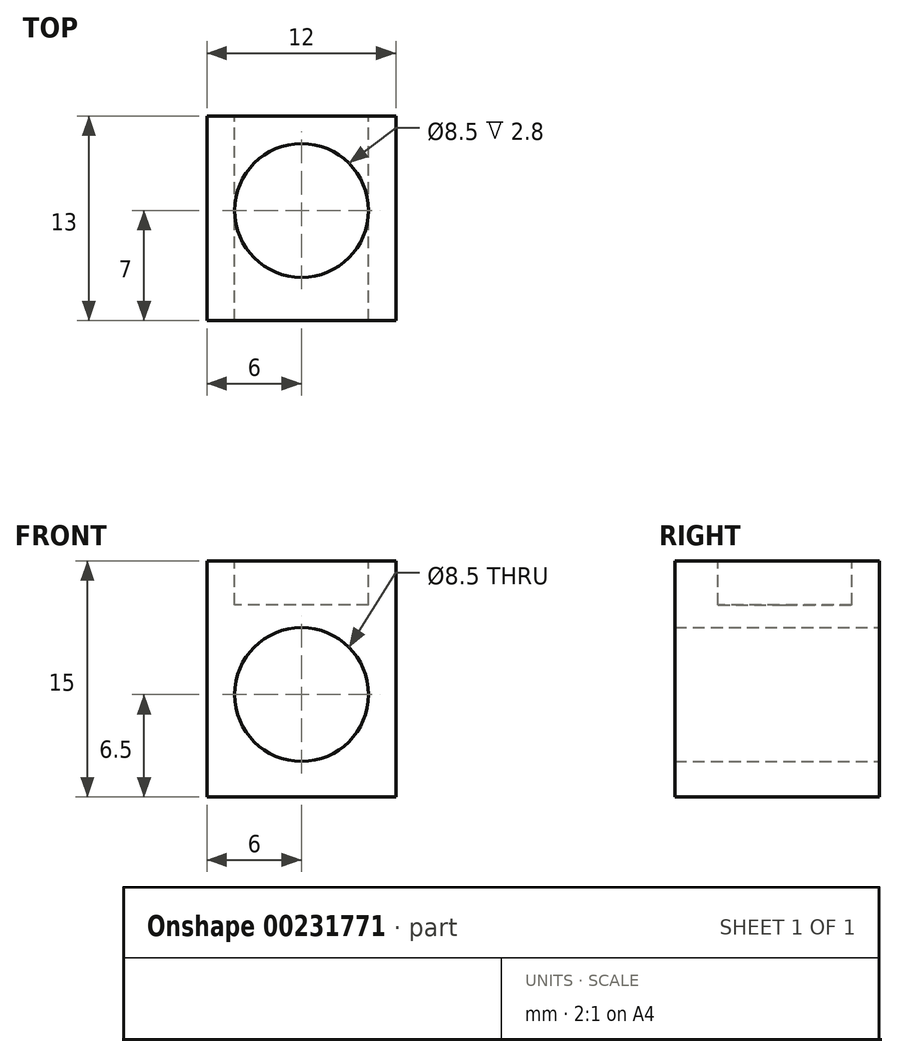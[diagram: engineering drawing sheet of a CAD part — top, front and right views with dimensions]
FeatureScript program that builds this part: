
annotation { "Feature Type Name" : "Feature", "Feature Type Description" : "" }
export const myFeature = defineFeature(function(context is Context, id is Id, definition is map)
    precondition{}
    {
        {
            var Q0;
            Q0=qCreatedBy(makeId("Front.planeOp"),FACE);
            var sketch = newSketch(context, id + "F0", { "sketchPlane" : qUnion([Q0])});
            skLineSegment(sketch, "E0.bottom", {"start": v(-6, 7.5) * mm, "end": v(6, 7.5) * mm});
            skLineSegment(sketch, "E0.top", {"start": v(-6, -7.5) * mm, "end": v(6, -7.5) * mm});
            skLineSegment(sketch, "E0.left", {"start": v(-6, 7.5) * mm, "end": v(-6, -7.5) * mm});
            skLineSegment(sketch, "E0.right", {"start": v(6, 7.5) * mm, "end": v(6, -7.5) * mm});
            skCircle(sketch, "E1", {"center": v(0, -1) * mm, "radius": 4.25 * mm});
            skSolve(sketch);
        }
        {
            var Q0;
            Q0=makeQuery(id+"F0.imprint","IMPRINT",FACE,{"disambiguationData":[TD([[makeQuery(id+"F0.imprint","IMPRINT",EDGE,{"derivedFrom":sQuery(id+"F0.wireOp",EDGE,"E0.bottom")}),-1.0]])]});
            extrude(context, id + "F1", {"entities" : qUnion([Q0]), "depth" : 24 * mm});
        }
        {
            var Q0;
            Q0=makeQuery(id+"F1.opExtrude","SWEPT_FACE",FACE,{"disambiguationData":[OSD([sQuery(id+"F0.wireOp",EDGE,"E0.bottom")])]});
            var sketch = newSketch(context, id + "F2", { "sketchPlane" : qUnion([Q0])});
            skCircle(sketch, "E2", {"center": v(0, -6) * mm, "radius": 4.12 * mm});
            skCircle(sketch, "E3", {"center": v(0, -17) * mm, "radius": 4.25 * mm});
            skSolve(sketch);
        }
        {
            var Q0;
            Q0=makeQuery(id+"F2.imprint","IMPRINT",FACE,{"disambiguationData":[TD([[makeQuery(id+"F2.imprint","IMPRINT",EDGE,{"derivedFrom":sQuery(id+"F2.wireOp",EDGE,"E2")}),1.0]])]});
            var Q1;
            Q1=makeQuery(id+"F2.imprint","IMPRINT",FACE,{"disambiguationData":[TD([[makeQuery(id+"F2.imprint","IMPRINT",EDGE,{"derivedFrom":sQuery(id+"F2.wireOp",EDGE,"E3")}),1.0]])]});
            extrude(context, id + "F3", {"entities" : qUnion([Q0, Q1]), "operationType" : NewBodyOperationType.REMOVE, "oppositeDirection" : true, "depth" : 2.8 * mm});
        }
        {
            var Q0;
            Q0=qCreatedBy(makeId("Front.planeOp"),FACE);
            cPlane(context, id + "F4", {"entities" : qUnion([Q0]), "cplaneType" : CPlaneType.OFFSET, "offset" : 11 * mm, "width" : 150 * mm, "height" : 150 * mm});
        }
        {
            var Q0;
            Q0=qCreatedBy(id+"F4.planeOp",FACE);
            var sketch = newSketch(context, id + "F5", { "sketchPlane" : qUnion([Q0])});
            skLineSegment(sketch, "E4.bottom", {"start": v(-11.27, -18.2) * mm, "end": v(11.56, -18.2) * mm});
            skLineSegment(sketch, "E4.top", {"start": v(-11.27, 26.25) * mm, "end": v(11.56, 26.25) * mm});
            skLineSegment(sketch, "E4.left", {"start": v(-11.27, -18.2) * mm, "end": v(-11.27, 26.25) * mm});
            skLineSegment(sketch, "E4.right", {"start": v(11.56, -18.2) * mm, "end": v(11.56, 26.25) * mm});
            skSolve(sketch);
        }
        {
            var Q0;
            Q0=makeQuery(id+"F5.imprint","IMPRINT",FACE,{"disambiguationData":[TD([[makeQuery(id+"F5.imprint","IMPRINT",EDGE,{"derivedFrom":sQuery(id+"F5.wireOp",EDGE,"E4.bottom")}),1.0]])]});
            extrude(context, id + "F6", {"entities" : qUnion([Q0]), "operationType" : NewBodyOperationType.REMOVE, "oppositeDirection" : true, "depth" : 25 * mm});
        }
    });
